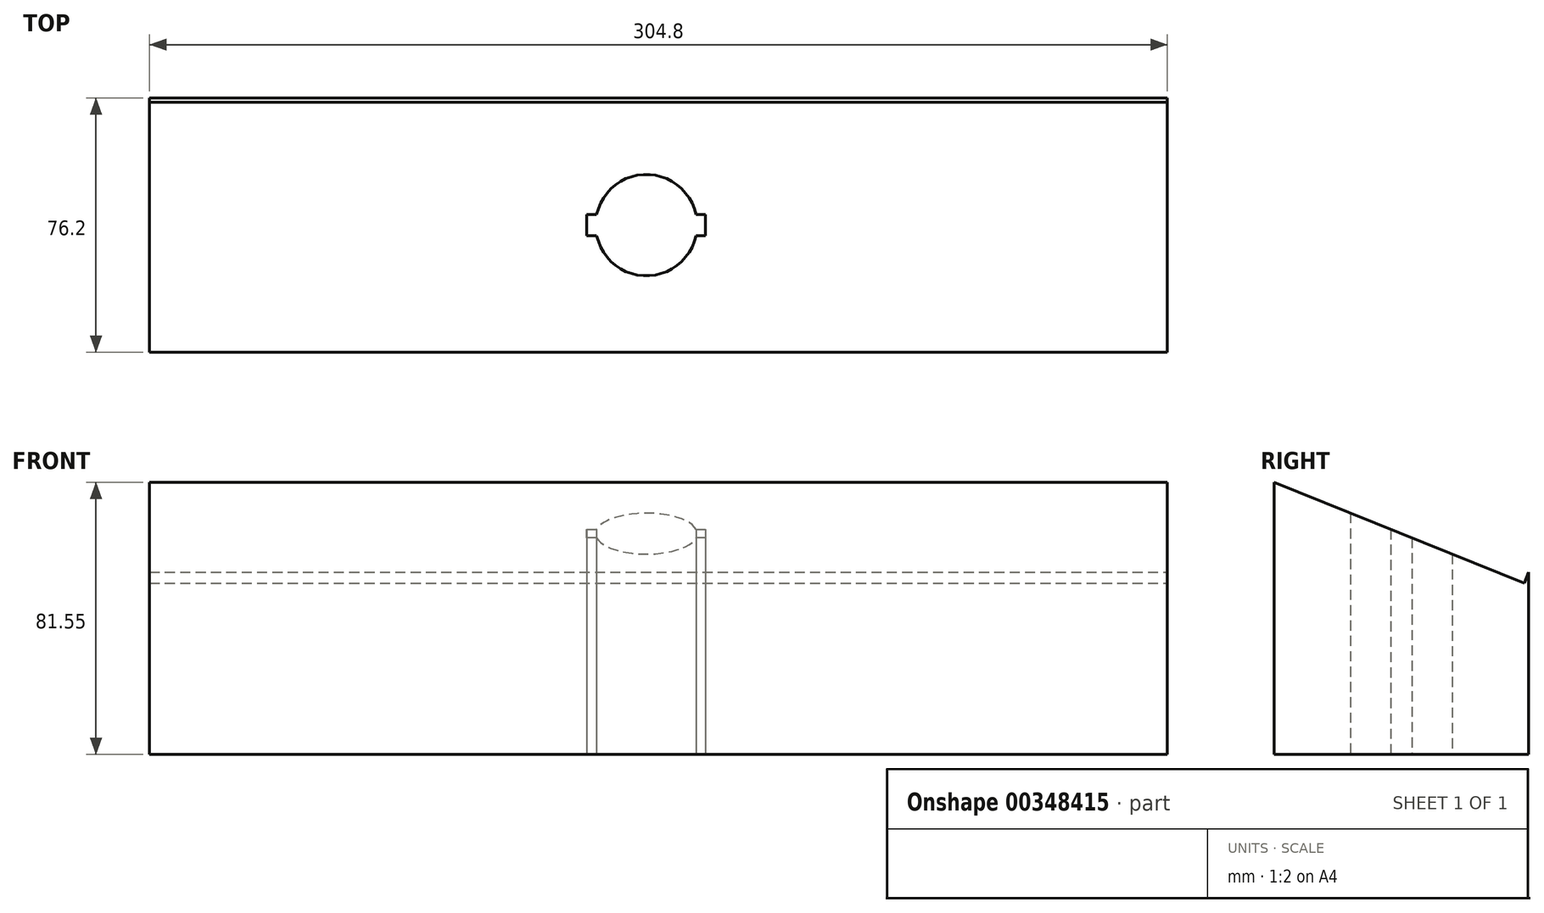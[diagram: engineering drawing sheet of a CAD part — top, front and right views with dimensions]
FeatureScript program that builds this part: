
annotation { "Feature Type Name" : "Feature", "Feature Type Description" : "" }
export const myFeature = defineFeature(function(context is Context, id is Id, definition is map)
    precondition{}
    {
        {
            var Q0;
            Q0=qCreatedBy(makeId("Right.planeOp"),FACE);
            var sketch = newSketch(context, id + "F0", { "sketchPlane" : qUnion([Q0])});
            skLineSegment(sketch, "E0", {"start": v(0, 0) * mm, "end": v(0, 81.55) * mm});
            skLineSegment(sketch, "E1", {"start": v(0, 81.55) * mm, "end": v(76.2, 50.8) * mm});
            skLineSegment(sketch, "E2", {"start": v(76.2, 50.8) * mm, "end": v(76.2, 0) * mm});
            skLineSegment(sketch, "E3", {"start": v(76.2, 0) * mm, "end": v(0, 0) * mm});
            skLineSegment(sketch, "E4", {"start": v(76.2, 50.8) * mm, "end": v(76.2, 54.6) * mm});
            skLineSegment(sketch, "E5", {"start": v(76.2, 54.6) * mm, "end": v(74.88, 51.33) * mm});
            skSolve(sketch);
        }
        {
            var Q0;
            Q0 = qSketchRegion(id + "F0", true);
            extrude(context, id + "F1", {"entities" : qUnion([Q0]), "oppositeDirection" : true, "depth" : 304.8 * mm});
        }
        {
            var Q0;
            Q0=qCreatedBy(makeId("Top.planeOp"),FACE);
            var sketch = newSketch(context, id + "F2", { "sketchPlane" : qUnion([Q0])});
            skCircle(sketch, "E6", {"center": v(-156.04, 38.1) * mm, "radius": 15.24 * mm});
            skSolve(sketch);
        }
        {
            var Q0;
            Q0 = qSketchRegion(id + "F2", true);
            extrude(context, id + "F3", {"entities" : qUnion([Q0]), "operationType" : NewBodyOperationType.REMOVE, "endBound" : BoundingType.THROUGH_ALL, "depth" : 25.4 * mm});
        }
        {
            var Q0;
            Q0=makeQuery(id+"F1.opExtrude","SWEPT_FACE",FACE,{"disambiguationData":[OSD([sQuery(id+"F0.wireOp",EDGE,"E3")])]});
            var sketch = newSketch(context, id + "F4", { "sketchPlane" : qUnion([Q0])});
            skLineSegment(sketch, "E7", {"start": v(-173.92, -34.93) * mm, "end": v(-138.36, -34.93) * mm});
            skLineSegment(sketch, "E8", {"start": v(-138.36, -34.93) * mm, "end": v(-138.36, -41.28) * mm});
            skLineSegment(sketch, "E9", {"start": v(-138.36, -41.28) * mm, "end": v(-173.92, -41.28) * mm});
            skLineSegment(sketch, "E10", {"start": v(-173.92, -41.28) * mm, "end": v(-173.92, -34.93) * mm});
            skSolve(sketch);
        }
        {
            var Q0;
            Q0 = qSketchRegion(id + "F4", true);
            extrude(context, id + "F5", {"entities" : qUnion([Q0]), "operationType" : NewBodyOperationType.REMOVE, "endBound" : BoundingType.THROUGH_ALL, "oppositeDirection" : true, "depth" : 25.4 * mm});
        }
    });
